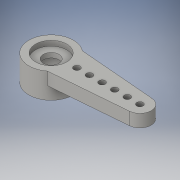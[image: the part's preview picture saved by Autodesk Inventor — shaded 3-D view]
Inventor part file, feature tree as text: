
AUTODESK INVENTOR PART (.ipt)
format: ipt  version: 2016 (Build 200138000, 138)  size: 161,792 bytes
history: native  units: in
note: dims shown in document units (in); Inventor stores cm internally (conversion verified against a paired STEP export)
features: mirror x1, sketch x1
ambient origin geometry x8: Origin, YZ Plane, XZ Plane, XY Plane, X Axis, Y Axis, Z Axis, Center Point
bodies: Solid1 (feature_tree)
feature tree (2):
  mirror  "Mirror1"
  sketch  "Sketch1"  dims[d0=0.5545in d1=0.0701in]
